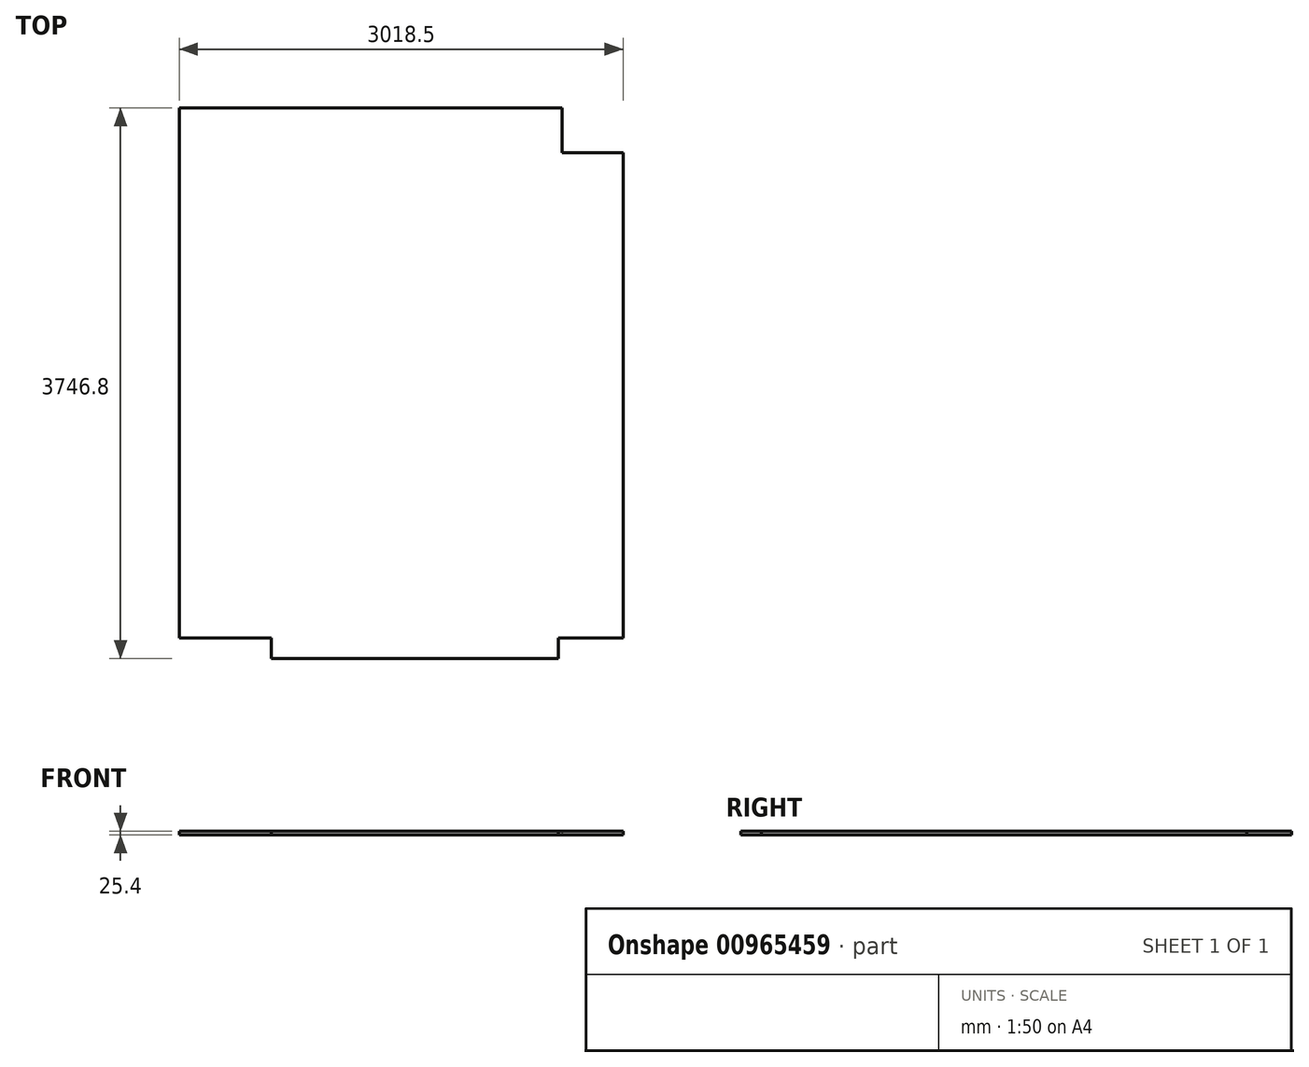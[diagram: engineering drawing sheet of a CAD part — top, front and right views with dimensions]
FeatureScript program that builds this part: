
annotation { "Feature Type Name" : "Feature", "Feature Type Description" : "" }
export const myFeature = defineFeature(function(context is Context, id is Id, definition is map)
    precondition{}
    {
        {
            var Q0;
            Q0=qCreatedBy(makeId("Top.planeOp"),FACE);
            var sketch = newSketch(context, id + "F0", { "sketchPlane" : qUnion([Q0])});
            skLineSegment(sketch, "E0", {"start": v(0, 0) * mm, "end": v(0, 3606.8) * mm});
            skLineSegment(sketch, "E1", {"start": v(0, 3606.8) * mm, "end": v(2603.5, 3606.8) * mm});
            skLineSegment(sketch, "E2", {"start": v(2603.5, 3606.8) * mm, "end": v(2603.5, 3301.8) * mm});
            skLineSegment(sketch, "E3", {"start": v(2603.5, 3301.8) * mm, "end": v(3018.5, 3301.8) * mm});
            skLineSegment(sketch, "E4", {"start": v(3018.5, 3301.8) * mm, "end": v(3018.5, 0) * mm});
            skLineSegment(sketch, "E5", {"start": v(0, 0) * mm, "end": v(625, 0) * mm});
            skLineSegment(sketch, "E6", {"start": v(3018.5, 0) * mm, "end": v(2578.5, 0) * mm});
            skLineSegment(sketch, "E7", {"start": v(625, 0) * mm, "end": v(625, -140) * mm});
            skLineSegment(sketch, "E8", {"start": v(625, -140) * mm, "end": v(2578.5, -140) * mm});
            skLineSegment(sketch, "E9", {"start": v(2578.5, -140) * mm, "end": v(2578.5, 0) * mm});
            skSolve(sketch);
        }
        {
            var Q0;
            Q0 = qSketchRegion(id + "F0", true);
            extrude(context, id + "F1", {"entities" : qUnion([Q0]), "depth" : 25.4 * mm, "offsetDistance" : 25.4 * mm});
        }
    });
